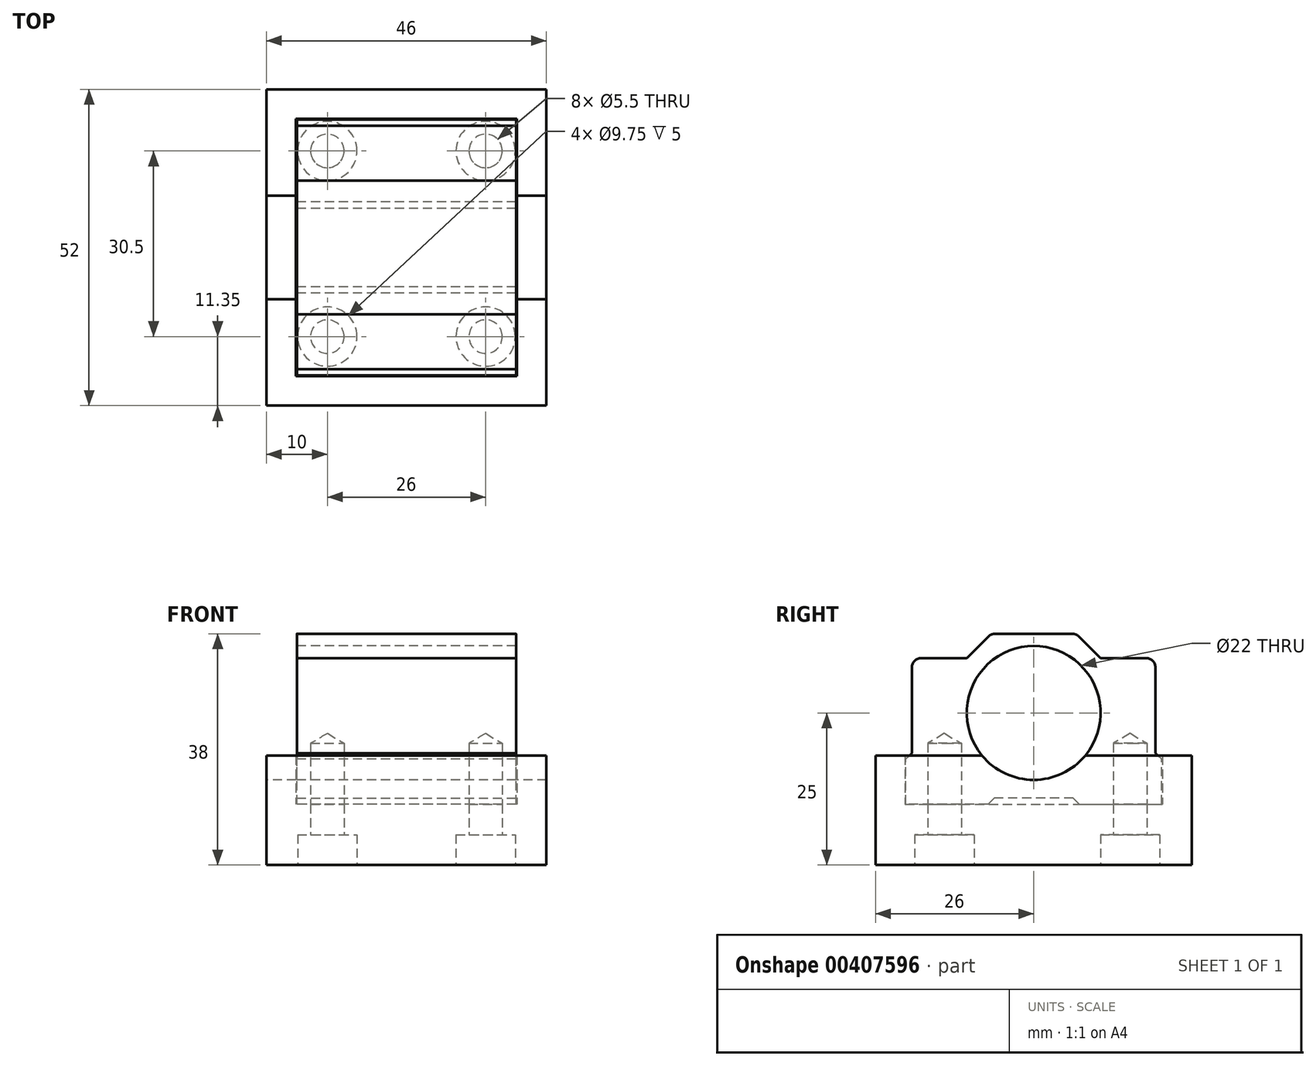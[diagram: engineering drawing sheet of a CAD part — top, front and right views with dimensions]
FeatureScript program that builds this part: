
annotation { "Feature Type Name" : "Feature", "Feature Type Description" : "" }
export const myFeature = defineFeature(function(context is Context, id is Id, definition is map)
    precondition{}
    {
        {
            assignVariable(context, id + "F0", {"name" : "lb1", "anyValue" : 36});
        }
        {
            var Q0;
            Q0=qCreatedBy(makeId("Right.planeOp"),FACE);
            var sketch = newSketch(context, id + "F1", { "sketchPlane" : qUnion([Q0])});
            skLineSegment(sketch, "E0", {"start": v(0, 33.56) * mm, "end": v(0, -18.3) * mm, "construction": true});
            skLineSegment(sketch, "E1", {"start": v(0, 0) * mm, "end": v(-7.5, 0) * mm});
            skLineSegment(sketch, "E2", {"start": v(-7.5, 0) * mm, "end": v(-7.5, -1) * mm});
            skLineSegment(sketch, "E3", {"start": v(-7.5, -1) * mm, "end": v(-21, -1) * mm});
            skLineSegment(sketch, "E4", {"start": v(-21, -1) * mm, "end": v(-21, 6.4) * mm});
            skLineSegment(sketch, "E5", {"start": v(-21, 6.4) * mm, "end": v(-20, 6.4) * mm});
            skLineSegment(sketch, "E6", {"start": v(-20, 6.4) * mm, "end": v(-20, 23) * mm});
            skLineSegment(sketch, "E7", {"start": v(-20, 23) * mm, "end": v(-11, 23) * mm});
            skLineSegment(sketch, "E8", {"start": v(-11, 23) * mm, "end": v(-7, 27) * mm});
            skLineSegment(sketch, "E9", {"start": v(-7, 27) * mm, "end": v(0, 27) * mm});
            skCircle(sketch, "E10", {"center": v(0, 14) * mm, "radius": 6 * mm});
            skCircle(sketch, "E11", {"center": v(0, 14) * mm, "radius": 11 * mm});
            skLineSegment(sketch, "E12.MirrorCS", {"start": v(7, 27) * mm, "end": v(0, 27) * mm});
            skLineSegment(sketch, "E13.MirrorCS", {"start": v(11, 23) * mm, "end": v(7, 27) * mm});
            skLineSegment(sketch, "E14.MirrorCS", {"start": v(20, 23) * mm, "end": v(11, 23) * mm});
            skLineSegment(sketch, "E15.MirrorCS", {"start": v(20, 6.4) * mm, "end": v(20, 23) * mm});
            skLineSegment(sketch, "E16.MirrorCS", {"start": v(21, 6.4) * mm, "end": v(20, 6.4) * mm});
            skLineSegment(sketch, "E17.MirrorCS", {"start": v(21, -1) * mm, "end": v(21, 6.4) * mm});
            skLineSegment(sketch, "E18.MirrorCS", {"start": v(7.5, -1) * mm, "end": v(21, -1) * mm});
            skLineSegment(sketch, "E19.MirrorCS", {"start": v(7.5, 0) * mm, "end": v(7.5, -1) * mm});
            skLineSegment(sketch, "E20.MirrorCS", {"start": v(0, 0) * mm, "end": v(7.5, 0) * mm});
            skSolve(sketch);
        }
        {
            var Q0;
            Q0=makeQuery(id+"F1.imprint","IMPRINT",FACE,{"disambiguationData":[TD([[makeQuery(id+"F1.imprint","IMPRINT",EDGE,{"derivedFrom":sQuery(id+"F1.wireOp",EDGE,"E1")}),-1.0]])]});
            extrude(context, id + "F2", {"entities" : qUnion([Q0]), "depth" : (getVariable(context, 'lb1')) * mm, "symmetric" : true});
        }
        {
            var Q0;
            Q0=makeQuery(id+"F1.imprint","IMPRINT",FACE,{"disambiguationData":[TD([[makeQuery(id+"F1.imprint","IMPRINT",EDGE,{"derivedFrom":sQuery(id+"F1.wireOp",EDGE,"E10")}),-1.0]])]});
            extrude(context, id + "F3", {"entities" : qUnion([Q0]), "depth" : (36 - 6) * mm, "symmetric" : true});
        }
        {
            var Q0;
            Q0=makeQuery(id+"F2.opExtrude","SWEPT_EDGE",EDGE,{"disambiguationData":[OSD([sQuery(id+"F1.wireOp",EDGE,"E5"),sQuery(id+"F1.wireOp",EDGE,"E6")])]});
            var Q1;
            Q1=makeQuery(id+"F2.opExtrude","SWEPT_EDGE",EDGE,{"disambiguationData":[OSD([sQuery(id+"F1.wireOp",EDGE,"E15.MirrorCS"),sQuery(id+"F1.wireOp",EDGE,"E16.MirrorCS")])]});
            var Q2;
            Q2=makeQuery(id+"F2.opExtrude","SWEPT_EDGE",EDGE,{"disambiguationData":[OSD([sQuery(id+"F1.wireOp",EDGE,"E1"),sQuery(id+"F1.wireOp",EDGE,"E2")])]});
            var Q3;
            Q3=makeQuery(id+"F2.opExtrude","SWEPT_EDGE",EDGE,{"disambiguationData":[OSD([sQuery(id+"F1.wireOp",EDGE,"E19.MirrorCS"),sQuery(id+"F1.wireOp",EDGE,"E20.MirrorCS")])]});
            chamfer(context, id + "F4", {"entities" : qUnion([Q0, Q1, Q2, Q3]), "width" : 1 * mm, "tangentPropagation" : true});
        }
        {
            var Q0;
            Q0=makeQuery(id+"F2.opExtrude","SWEPT_EDGE",EDGE,{"disambiguationData":[OSD([sQuery(id+"F1.wireOp",EDGE,"E8"),sQuery(id+"F1.wireOp",EDGE,"E9")])]});
            var Q1;
            Q1=makeQuery(id+"F2.opExtrude","SWEPT_EDGE",EDGE,{"disambiguationData":[OSD([sQuery(id+"F1.wireOp",EDGE,"E12.MirrorCS"),sQuery(id+"F1.wireOp",EDGE,"E13.MirrorCS")])]});
            var Q2;
            Q2=makeQuery(id+"F2.opExtrude","SWEPT_EDGE",EDGE,{"disambiguationData":[OSD([sQuery(id+"F1.wireOp",EDGE,"E6"),sQuery(id+"F1.wireOp",EDGE,"E7")])]});
            var Q3;
            Q3=makeQuery(id+"F2.opExtrude","SWEPT_EDGE",EDGE,{"disambiguationData":[OSD([sQuery(id+"F1.wireOp",EDGE,"E14.MirrorCS"),sQuery(id+"F1.wireOp",EDGE,"E15.MirrorCS")])]});
            fillet(context, id + "F5", {"entities" : qUnion([Q0, Q1, Q2, Q3]), "radius" : 1.5 * mm, "tangentPropagation" : true, "allowEdgeOverflow" : false});
        }
        {
            var Q0;
            Q0=makeQuery(id+"F2.opExtrude","SWEPT_FACE",FACE,{"disambiguationData":[OSD([sQuery(id+"F1.wireOp",EDGE,"E3")])]});
            var sketch = newSketch(context, id + "F6", { "sketchPlane" : qUnion([Q0])});
            skLineSegment(sketch, "E21.bottom", {"start": v(13, 14.65) * mm, "end": v(-13, 14.65) * mm});
            skLineSegment(sketch, "E21.top", {"start": v(13, -15.85) * mm, "end": v(-13, -15.85) * mm});
            skLineSegment(sketch, "E21.left", {"start": v(13, 14.65) * mm, "end": v(13, -15.85) * mm});
            skLineSegment(sketch, "E21.right", {"start": v(-13, 14.65) * mm, "end": v(-13, -15.85) * mm});
            skLineSegment(sketch, "E22.bottom", {"start": v(-23, -26) * mm, "end": v(23, -26) * mm});
            skLineSegment(sketch, "E22.top", {"start": v(-23, 26) * mm, "end": v(23, 26) * mm});
            skLineSegment(sketch, "E22.left", {"start": v(-23, -26) * mm, "end": v(-23, 26) * mm});
            skLineSegment(sketch, "E22.right", {"start": v(23, -26) * mm, "end": v(23, 26) * mm});
            skPoint(sketch, "E22.middle", {"position": v(0, 0) * mm});
            skLineSegment(sketch, "E23.bottom", {"start": v(18, 21) * mm, "end": v(-18, 21) * mm});
            skLineSegment(sketch, "E23.top", {"start": v(18, -21) * mm, "end": v(-18, -21) * mm});
            skLineSegment(sketch, "E23.left", {"start": v(18, 21) * mm, "end": v(18, -21) * mm});
            skLineSegment(sketch, "E23.right", {"start": v(-18, 21) * mm, "end": v(-18, -21) * mm});
            skLineSegment(sketch, "E24.bottom", {"start": v(18.15, 21.15) * mm, "end": v(-18.15, 21.15) * mm});
            skLineSegment(sketch, "E24.top", {"start": v(18.15, -21.15) * mm, "end": v(-18.15, -21.15) * mm});
            skLineSegment(sketch, "E24.left", {"start": v(18.15, 21.15) * mm, "end": v(18.15, -21.15) * mm});
            skLineSegment(sketch, "E24.right", {"start": v(-18.15, 21.15) * mm, "end": v(-18.15, -21.15) * mm});
            skSolve(sketch);
        }
        {
            var Q0;
            {var subQ1=sQuery(id+"F6.wireOp",EDGE,"E21.bottom");Q0=makeQuery(id+"F6.imprint","IMPRINT",FACE,{"disambiguationData":[TD([[makeQuery(id+"F6.imprint","IMPRINT",EDGE,{"derivedFrom":subQ1}),-1.0]])]});}
            var Q1;
            {var subQ0=sQuery(id+"F6.wireOp",EDGE,"E21.top");Q1=makeQuery(id+"F6.imprint","IMPRINT",FACE,{"disambiguationData":[TD([[makeQuery(id+"F6.imprint","IMPRINT",EDGE,{"derivedFrom":subQ0}),-1.0]])]});}
            var Q2;
            {var subQ0=sQuery(id+"F6.wireOp",EDGE,"E21.bottom");Q2=makeQuery(id+"F6.imprint","IMPRINT",FACE,{"disambiguationData":[TD([[makeQuery(id+"F6.imprint","IMPRINT",EDGE,{"derivedFrom":subQ0}),1.0]])]});}
            var Q3;
            {var subQ1=sQuery(id+"F6.wireOp",EDGE,"E21.top");Q3=makeQuery(id+"F6.imprint","IMPRINT",FACE,{"disambiguationData":[TD([[makeQuery(id+"F6.imprint","IMPRINT",EDGE,{"derivedFrom":subQ1}),1.0]])]});}
            var Q4;
            {var subQ1=sQuery(id+"F6.wireOp",EDGE,"E23.bottom");Q4=makeQuery(id+"F6.imprint","IMPRINT",FACE,{"disambiguationData":[TD([[makeQuery(id+"F6.imprint","IMPRINT",EDGE,{"derivedFrom":subQ1}),-1.0]])]});}
            var Q5;
            Q5=makeQuery(id+"F6.imprint","IMPRINT",FACE,{"disambiguationData":[TD([[makeQuery(id+"F6.imprint","IMPRINT",EDGE,{"derivedFrom":sQuery(id+"F6.wireOp",EDGE,"E22.bottom")}),1.0]])]});
            extrude(context, id + "F7", {"entities" : qUnion([Q0, Q1, Q2, Q3, Q4, Q5]), "depth" : 10 * mm});
        }
        {
            var Q0;
            Q0=makeQuery(id+"F6.imprint","IMPRINT",FACE,{"disambiguationData":[TD([[makeQuery(id+"F6.imprint","IMPRINT",EDGE,{"derivedFrom":sQuery(id+"F6.wireOp",EDGE,"E22.bottom")}),1.0]])]});
            extrude(context, id + "F8", {"entities" : qUnion([Q0]), "operationType" : NewBodyOperationType.ADD, "oppositeDirection" : true, "depth" : 8 * mm});
        }
        {
            var Q0;
            Q0=makeQuery(id+"F7.opExtrude","CAP_FACE",FACE,{"disambiguationData":[OSD([sQuery(id+"F6.wireOp",EDGE,"E22.bottom"),sQuery(id+"F6.wireOp",EDGE,"E22.top"),sQuery(id+"F6.wireOp",EDGE,"E22.left"),sQuery(id+"F6.wireOp",EDGE,"E22.right")])],"isStart":false});
            var sketch = newSketch(context, id + "F9", { "sketchPlane" : qUnion([Q0])});
            skPoint(sketch, "E25.0", {"position": v(-13, 14.65) * mm});
            skLineSegment(sketch, "E26.0.0", {"start": v(23, 26) * mm, "end": v(-23, 26) * mm});
            skLineSegment(sketch, "E26.0.1", {"start": v(-23, 26) * mm, "end": v(-23, -26) * mm});
            skLineSegment(sketch, "E26.0.2", {"start": v(-23, -26) * mm, "end": v(23, -26) * mm});
            skLineSegment(sketch, "E26.0.3", {"start": v(23, -26) * mm, "end": v(23, 26) * mm});
            skPoint(sketch, "E27.0", {"position": v(13, 14.65) * mm});
            skPoint(sketch, "E28.0", {"position": v(-13, -15.85) * mm});
            skPoint(sketch, "E29.0", {"position": v(13, -15.85) * mm});
            skSolve(sketch);
        }
        {
            var Q0;
            Q0=sQuery(id+"F9.wireOp",VERTEX,"E28.0");
            var Q1;
            Q1=sQuery(id+"F9.wireOp",VERTEX,"E29.0");
            var Q2;
            Q2=sQuery(id+"F9.wireOp",VERTEX,"E25.0");
            var Q3;
            Q3=sQuery(id+"F9.wireOp",VERTEX,"E27.0");
            var Q4;
            Q4=makeQuery(id+"F7.opExtrude","SWEPT_BODY",BODY,{"disambiguationData":[OSD([sQuery(id+"F6.wireOp",EDGE,"E22.bottom"),sQuery(id+"F6.wireOp",EDGE,"E22.top"),sQuery(id+"F6.wireOp",EDGE,"E22.left"),sQuery(id+"F6.wireOp",EDGE,"E22.right")])]});
            var Q5;
            Q5=makeQuery(id+"F2.opExtrude","SWEPT_BODY",BODY,{"disambiguationData":[OSD([sQuery(id+"F1.wireOp",EDGE,"E1"),sQuery(id+"F1.wireOp",EDGE,"E2"),sQuery(id+"F1.wireOp",EDGE,"E3"),sQuery(id+"F1.wireOp",EDGE,"E4"),sQuery(id+"F1.wireOp",EDGE,"E5"),sQuery(id+"F1.wireOp",EDGE,"E6"),sQuery(id+"F1.wireOp",EDGE,"E7"),sQuery(id+"F1.wireOp",EDGE,"E8"),sQuery(id+"F1.wireOp",EDGE,"E9"),sQuery(id+"F1.wireOp",EDGE,"E11"),sQuery(id+"F1.wireOp",EDGE,"E12.MirrorCS"),sQuery(id+"F1.wireOp",EDGE,"E13.MirrorCS"),sQuery(id+"F1.wireOp",EDGE,"E14.MirrorCS"),sQuery(id+"F1.wireOp",EDGE,"E15.MirrorCS"),sQuery(id+"F1.wireOp",EDGE,"E16.MirrorCS"),sQuery(id+"F1.wireOp",EDGE,"E17.MirrorCS"),sQuery(id+"F1.wireOp",EDGE,"E18.MirrorCS"),sQuery(id+"F1.wireOp",EDGE,"E19.MirrorCS"),sQuery(id+"F1.wireOp",EDGE,"E20.MirrorCS")])]});
            hole(context, id + "F10", {"style" : HoleStyle.C_BORE, "endStyle" : HoleEndStyle.BLIND, "standardTappedOrClearance" : lookupTablePath({ "standard" : "ISO", "fit" : "Normal", "size" : "M5", "type" : "Clearance" }), "standardBlindInLast" : lookupTablePath({ "fit" : "Standard", "standard" : "ISO", "size" : "M5", "type" : "Clearance" }), "holeDiameter" : 5.5 * mm, "cBoreDiameter" : 9.75 * mm, "cBoreDepth" : 5 * mm, "holeDepth" : 20 * mm, "tappedDepth" : 14 * mm, "tapClearance" : 3, "locations" : qUnion([Q0, Q1, Q2, Q3]), "scope" : qUnion([Q4, Q5])});
        }
        {
            var Q0;
            Q0=makeQuery(id+"F1.imprint","IMPRINT",FACE,{"disambiguationData":[TD([[makeQuery(id+"F1.imprint","IMPRINT",EDGE,{"derivedFrom":sQuery(id+"F1.wireOp",EDGE,"E10")}),-1.0]])]});
            var Q1;
            Q1=makeQuery(id+"F1.imprint","IMPRINT",FACE,{"disambiguationData":[TD([[makeQuery(id+"F1.imprint","IMPRINT",EDGE,{"derivedFrom":sQuery(id+"F1.wireOp",EDGE,"E10")}),1.0]])]});
            extrude(context, id + "F11", {"entities" : qUnion([Q0, Q1]), "operationType" : NewBodyOperationType.REMOVE, "depth" : 115.6 * mm, "symmetric" : true});
        }
    });
